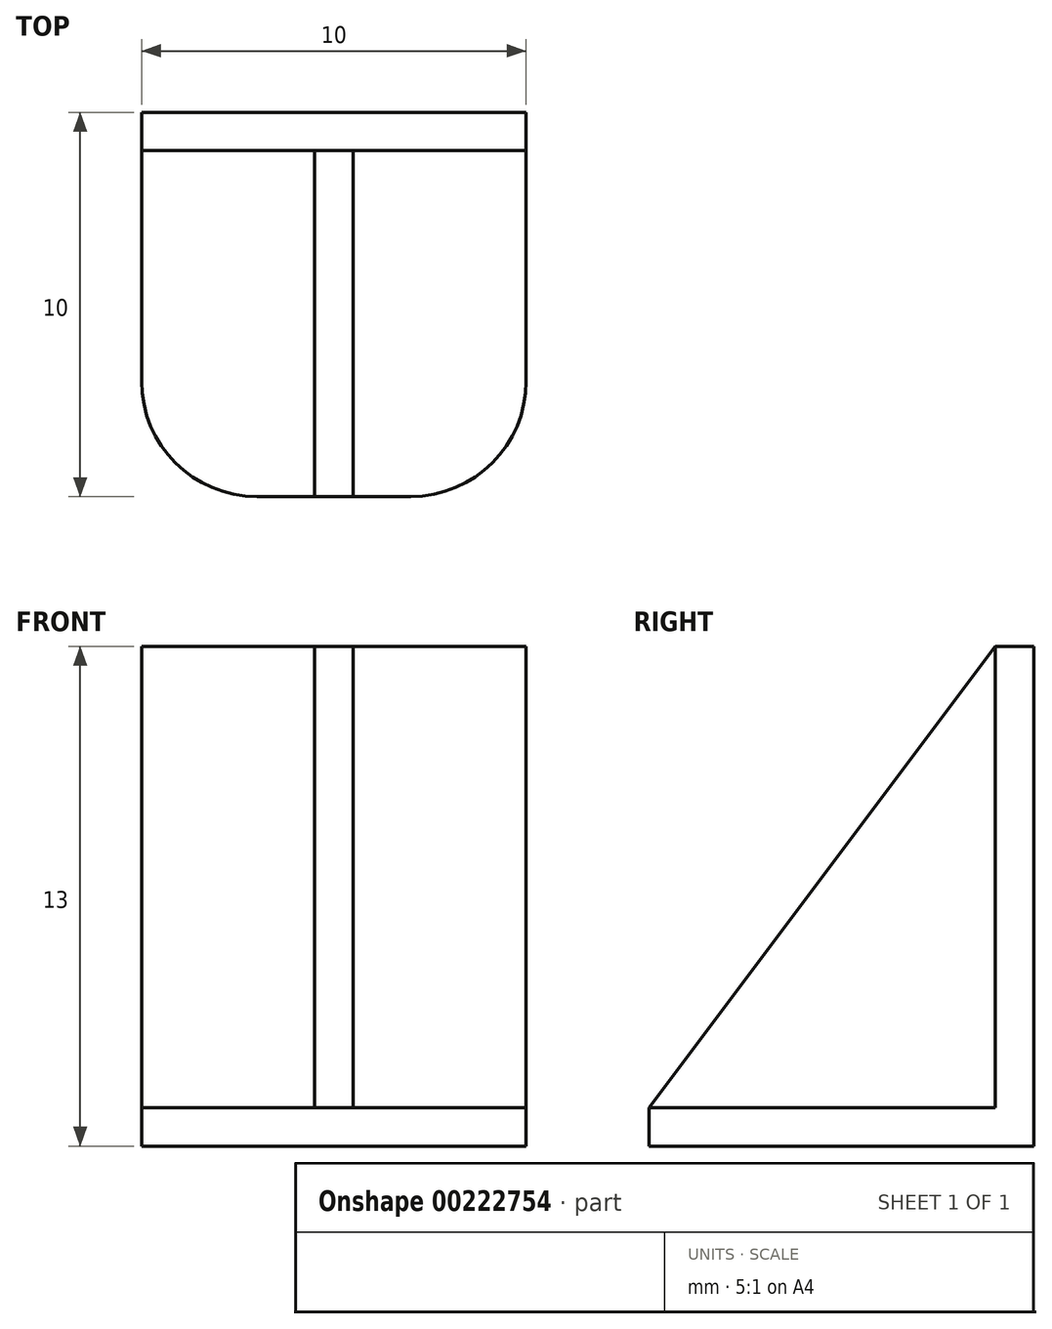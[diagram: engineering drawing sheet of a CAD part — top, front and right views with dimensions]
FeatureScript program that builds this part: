
annotation { "Feature Type Name" : "Feature", "Feature Type Description" : "" }
export const myFeature = defineFeature(function(context is Context, id is Id, definition is map)
    precondition{}
    {
        {
            assignVariable(context, id + "F0", {"name" : "Hoehe", "anyValue" : 12});
        }
        {
            var Q0;
            Q0=qCreatedBy(makeId("Top.planeOp"),FACE);
            var sketch = newSketch(context, id + "F1", { "sketchPlane" : qUnion([Q0])});
            skLineSegment(sketch, "E0.bottom", {"start": v(3.65, 10) * mm, "end": v(-6.35, 10) * mm});
            skLineSegment(sketch, "E0.top", {"start": v(3.65, 0) * mm, "end": v(-6.35, 0) * mm});
            skLineSegment(sketch, "E0.left", {"start": v(3.65, 10) * mm, "end": v(3.65, 0) * mm});
            skLineSegment(sketch, "E0.right", {"start": v(-6.35, 10) * mm, "end": v(-6.35, 0) * mm});
            skSolve(sketch);
        }
        {
            var Q0;
            Q0 = qSketchRegion(id + "F1", true);
            extrude(context, id + "F2", {"entities" : qUnion([Q0]), "depth" : 1 * mm});
        }
        {
            var Q0;
            Q0=makeQuery(id+"F2.opExtrude","CAP_FACE",FACE,{"disambiguationData":[OSD([sQuery(id+"F1.wireOp",EDGE,"E0.bottom"),sQuery(id+"F1.wireOp",EDGE,"E0.top"),sQuery(id+"F1.wireOp",EDGE,"E0.left"),sQuery(id+"F1.wireOp",EDGE,"E0.right")])],"isStart":false});
            var sketch = newSketch(context, id + "F3", { "sketchPlane" : qUnion([Q0])});
            skLineSegment(sketch, "E1.bottom", {"start": v(-6.35, 10) * mm, "end": v(3.65, 10) * mm});
            skLineSegment(sketch, "E1.top", {"start": v(-6.35, 9) * mm, "end": v(3.65, 9) * mm});
            skLineSegment(sketch, "E1.left", {"start": v(-6.35, 10) * mm, "end": v(-6.35, 9) * mm});
            skLineSegment(sketch, "E1.right", {"start": v(3.65, 10) * mm, "end": v(3.65, 9) * mm});
            skSolve(sketch);
        }
        {
            var Q0;
            Q0 = qSketchRegion(id + "F3", true);
            extrude(context, id + "F4", {"entities" : qUnion([Q0]), "operationType" : NewBodyOperationType.ADD, "depth" : (getVariable(context, 'Hoehe')) * mm});
        }
        {
            var Q0;
            Q0=makeQuery(id+"F4.opExtrude","SWEPT_FACE",FACE,{"disambiguationData":[OSD([sQuery(id+"F3.wireOp",EDGE,"E1.top")])]});
            var sketch = newSketch(context, id + "F5", { "sketchPlane" : qUnion([Q0])});
            skLineSegment(sketch, "E2.bottom", {"start": v(-1.85, 13) * mm, "end": v(-0.85, 13) * mm});
            skLineSegment(sketch, "E2.top", {"start": v(-1.85, 1) * mm, "end": v(-0.85, 1) * mm});
            skLineSegment(sketch, "E2.left", {"start": v(-1.85, 13) * mm, "end": v(-1.85, 1) * mm});
            skLineSegment(sketch, "E2.right", {"start": v(-0.85, 13) * mm, "end": v(-0.85, 1) * mm});
            skSolve(sketch);
        }
        {
            var Q0;
            Q0=makeQuery(id+"F2.opExtrude","CAP_FACE",FACE,{"disambiguationData":[OSD([sQuery(id+"F1.wireOp",EDGE,"E0.bottom"),sQuery(id+"F1.wireOp",EDGE,"E0.top"),sQuery(id+"F1.wireOp",EDGE,"E0.left"),sQuery(id+"F1.wireOp",EDGE,"E0.right")])],"isStart":false});
            var sketch = newSketch(context, id + "F6", { "sketchPlane" : qUnion([Q0])});
            skLineSegment(sketch, "E3.bottom", {"start": v(-1.85, 0) * mm, "end": v(-0.85, 0) * mm});
            skLineSegment(sketch, "E3.top", {"start": v(-1.85, 9) * mm, "end": v(-0.85, 9) * mm});
            skLineSegment(sketch, "E3.left", {"start": v(-1.85, 0) * mm, "end": v(-1.85, 9) * mm});
            skLineSegment(sketch, "E3.right", {"start": v(-0.85, 0) * mm, "end": v(-0.85, 9) * mm});
            skPoint(sketch, "E4.0", {"position": v(-0.85, 9) * mm});
            skPoint(sketch, "E5.0", {"position": v(-1.85, 9) * mm});
            skSolve(sketch);
        }
        {
            var Q0;
            Q0=sQuery(id+"F5.wireOp",VERTEX,"E2.left.start");
            var Q1;
            Q1=sQuery(id+"F6.wireOp",VERTEX,"E3.left.start");
            var Q2;
            Q2=sQuery(id+"F6.wireOp",VERTEX,"E3.right.start");
            cPlane(context, id + "F7", {"entities" : qUnion([Q0, Q1, Q2]), "cplaneType" : CPlaneType.THREE_POINT, "offset" : 25 * mm, "width" : 150 * mm, "height" : 150 * mm});
        }
        {
            var Q0;
            Q0=qCreatedBy(id+"F7.planeOp",FACE);
            var sketch = newSketch(context, id + "F8", { "sketchPlane" : qUnion([Q0])});
            skPoint(sketch, "E6.0", {"position": v(1.85, 15.8) * mm});
            skPoint(sketch, "E7.0", {"position": v(0.85, 15.8) * mm});
            skPoint(sketch, "E8.0", {"position": v(0.85, 0.8) * mm});
            skPoint(sketch, "E9.0", {"position": v(1.85, 0.8) * mm});
            skLineSegment(sketch, "E10", {"start": v(1.85, 15.8) * mm, "end": v(0.85, 15.8) * mm});
            skLineSegment(sketch, "E11", {"start": v(0.85, 15.8) * mm, "end": v(0.85, 0.8) * mm});
            skLineSegment(sketch, "E12", {"start": v(1.85, 0.8) * mm, "end": v(0.85, 0.8) * mm});
            skLineSegment(sketch, "E13", {"start": v(1.85, 0.8) * mm, "end": v(1.85, 15.8) * mm});
            skSolve(sketch);
        }
        {
            var Q0;
            Q0 = qSketchRegion(id + "F8", true);
            extrude(context, id + "F9", {"entities" : qUnion([Q0]), "operationType" : NewBodyOperationType.ADD, "endBound" : BoundingType.UP_TO_NEXT, "depth" : 25 * mm});
        }
        {
            var Q0;
            Q0=makeQuery(id+"F2.opExtrude","SWEPT_EDGE",EDGE,{"disambiguationData":[OSD([sQuery(id+"F1.wireOp",EDGE,"E0.top"),sQuery(id+"F1.wireOp",EDGE,"E0.left")])]});
            var Q1;
            Q1=makeQuery(id+"F2.opExtrude","SWEPT_EDGE",EDGE,{"disambiguationData":[OSD([sQuery(id+"F1.wireOp",EDGE,"E0.top"),sQuery(id+"F1.wireOp",EDGE,"E0.right")])]});
            fillet(context, id + "F10", {"entities" : qUnion([Q0, Q1]), "radius" : 3 * mm, "tangentPropagation" : true, "allowEdgeOverflow" : false});
        }
    });
